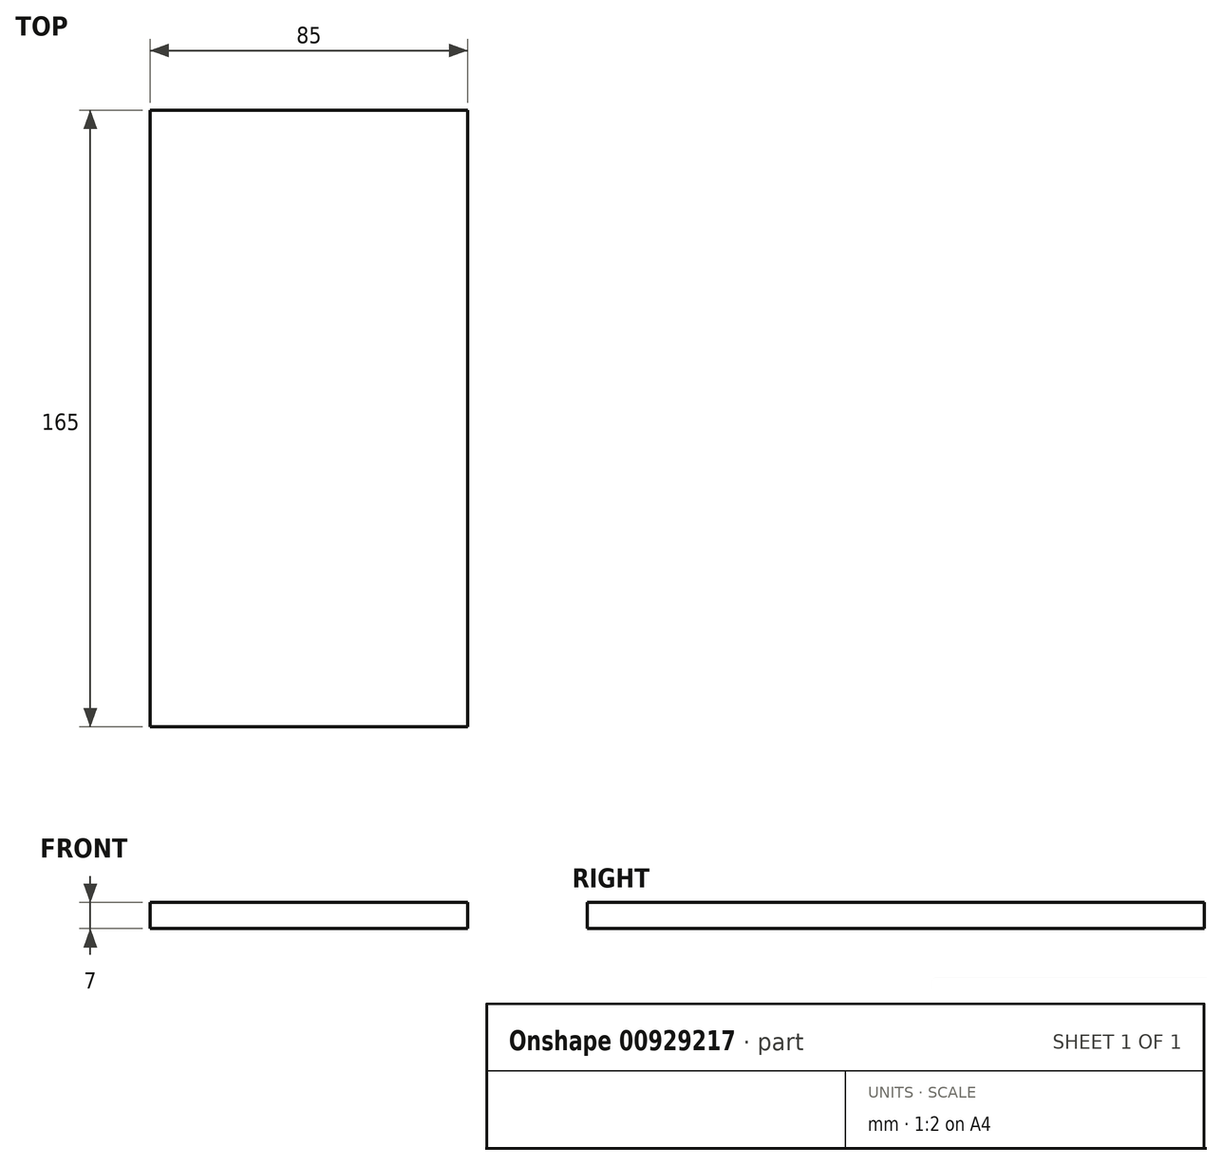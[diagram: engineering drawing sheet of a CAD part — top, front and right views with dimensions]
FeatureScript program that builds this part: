
annotation { "Feature Type Name" : "Feature", "Feature Type Description" : "" }
export const myFeature = defineFeature(function(context is Context, id is Id, definition is map)
    precondition{}
    {
        {
            var Q0;
            Q0=qCreatedBy(makeId("Front.planeOp"),FACE);
            var sketch = newSketch(context, id + "F0", { "sketchPlane" : qUnion([Q0])});
            skLineSegment(sketch, "E0.bottom", {"start": v(42.5, 3.5) * mm, "end": v(-42.5, 3.5) * mm});
            skLineSegment(sketch, "E0.top", {"start": v(42.5, -3.5) * mm, "end": v(-42.5, -3.5) * mm});
            skLineSegment(sketch, "E0.left", {"start": v(42.5, 3.5) * mm, "end": v(42.5, -3.5) * mm});
            skLineSegment(sketch, "E0.right", {"start": v(-42.5, 3.5) * mm, "end": v(-42.5, -3.5) * mm});
            skPoint(sketch, "E0.middle", {"position": v(0, 0) * mm});
            skSolve(sketch);
        }
        {
            var Q0;
            Q0 = qSketchRegion(id + "F0", true);
            extrude(context, id + "F1", {"entities" : qUnion([Q0]), "endBound" : BoundingType.SYMMETRIC, "depth" : 165 * mm, "offsetDistance" : 25 * mm});
        }
    });
